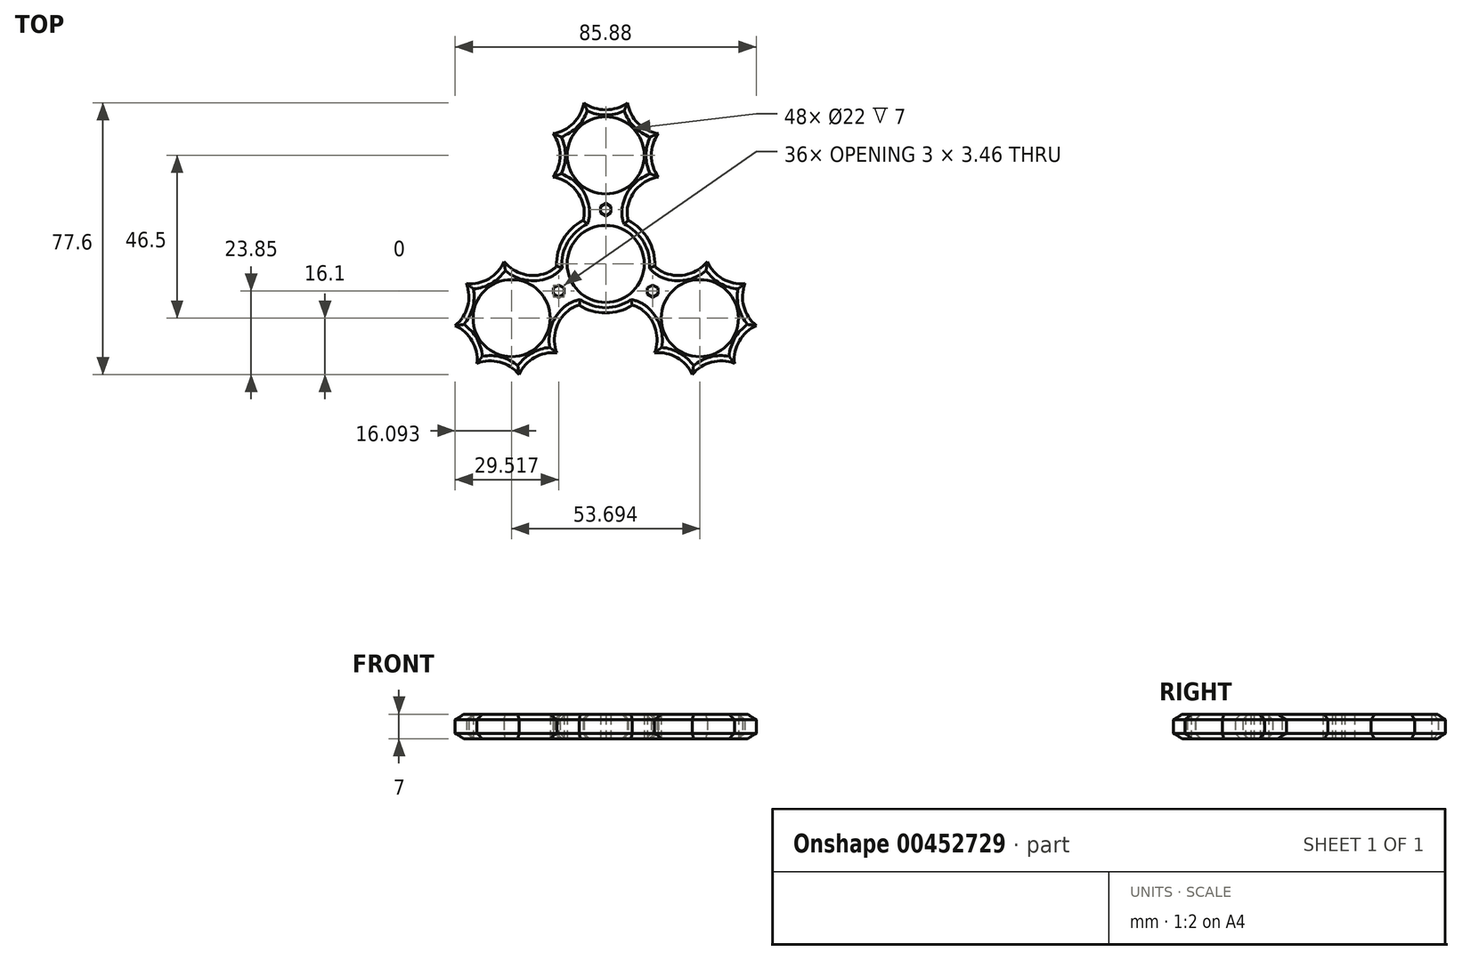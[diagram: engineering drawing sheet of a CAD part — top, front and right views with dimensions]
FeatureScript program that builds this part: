
annotation { "Feature Type Name" : "Feature", "Feature Type Description" : "" }
export const myFeature = defineFeature(function(context is Context, id is Id, definition is map)
    precondition{}
    {
        {
            var Q0;
            Q0=qCreatedBy(makeId("Top.planeOp"),FACE);
            var sketch = newSketch(context, id + "F0", { "sketchPlane" : qUnion([Q0])});
            skCircle(sketch, "E0", {"center": v(0, 0) * mm, "radius": 11 * mm});
            skArc(sketch, "E1.0", {"start": v(-6.44, 12.43) * mm, "mid": v(0, -14) * mm, "end": v(6.44, 12.43) * mm});
            skLineSegment(sketch, "E2", {"start": v(0, 11) * mm, "end": v(0, 20) * mm});
            skCircle(sketch, "E3", {"center": v(0, 31) * mm, "radius": 11 * mm});
            skPoint(sketch, "E4.0.midPoint", {"position": v(0, 45) * mm});
            skLineSegment(sketch, "E5", {"start": v(-15, 24.79) * mm, "end": v(0, 31) * mm});
            skLineSegment(sketch, "E6", {"start": v(-6.21, 16) * mm, "end": v(0, 31) * mm});
            skPoint(sketch, "E7", {"position": v(-9.2, 21.8) * mm});
            skArc(sketch, "E8", {"start": v(-6.21, 16) * mm, "mid": v(-9.2, 21.8) * mm, "end": v(-15, 24.79) * mm});
            skArc(sketch, "E9.1.0", {"start": v(-15, 24.79) * mm, "mid": v(-13, 31) * mm, "end": v(-15, 37.21) * mm});
            skArc(sketch, "E9.2.0", {"start": v(-15, 37.21) * mm, "mid": v(-9.2, 40.2) * mm, "end": v(-6.21, 46) * mm});
            skArc(sketch, "E9.3.0", {"start": v(-6.21, 46) * mm, "mid": v(0, 44) * mm, "end": v(6.21, 46) * mm});
            skArc(sketch, "E9.4.0", {"start": v(6.21, 46) * mm, "mid": v(9.2, 40.2) * mm, "end": v(15, 37.21) * mm});
            skArc(sketch, "E9.5.0", {"start": v(15, 37.21) * mm, "mid": v(13, 31) * mm, "end": v(15, 24.79) * mm});
            skArc(sketch, "E9.6.0", {"start": v(15, 24.79) * mm, "mid": v(9.2, 21.8) * mm, "end": v(6.21, 16) * mm});
            skLineSegment(sketch, "E9.anchor1", {"start": v(0, 31) * mm, "end": v(-16.72, 14.28) * mm, "construction": true});
            skLineSegment(sketch, "E9.anchor2", {"start": v(0, 31) * mm, "end": v(16.72, 14.28) * mm, "construction": true});
            skPoint(sketch, "E10.orphan", {"position": v(-15, 36.21) * mm});
            skPoint(sketch, "E11.orphan", {"position": v(-6.21, 45) * mm});
            skPoint(sketch, "E12.orphan", {"position": v(6.21, 45) * mm});
            skPoint(sketch, "E13.orphan", {"position": v(15, 36.21) * mm});
            skPoint(sketch, "E14.orphan", {"position": v(15, 23.79) * mm});
            skLineSegment(sketch, "E15", {"start": v(9.53, 5.5) * mm, "end": v(12.12, 7) * mm});
            skArc(sketch, "E16", {"start": v(6.21, 16) * mm, "mid": v(7.41, 10.35) * mm, "end": v(12.12, 7) * mm});
            skArc(sketch, "E17.MirrorCS", {"start": v(-6.21, 16) * mm, "mid": v(-7.41, 10.35) * mm, "end": v(-12.12, 7) * mm});
            skArc(sketch, "E18.1.0", {"start": v(-24.73, -31.6) * mm, "mid": v(-30.21, -28.06) * mm, "end": v(-36.73, -28.38) * mm});
            skPoint(sketch, "E18.1.1", {"position": v(-26.85, -15.5) * mm});
            skArc(sketch, "E18.1.2", {"start": v(-42.94, -17.62) * mm, "mid": v(-39.4, -12.14) * mm, "end": v(-39.73, -5.62) * mm});
            skPoint(sketch, "E18.1.3", {"position": v(-42.08, -17.12) * mm});
            skPoint(sketch, "E18.1.4", {"position": v(-28.1, 1.1) * mm});
            skArc(sketch, "E18.1.5", {"start": v(-13.97, -25.38) * mm, "mid": v(-20.35, -26.76) * mm, "end": v(-24.73, -31.6) * mm});
            skArc(sketch, "E18.1.6", {"start": v(-39.73, -5.62) * mm, "mid": v(-33.35, -4.24) * mm, "end": v(-28.97, 0.6) * mm});
            skPoint(sketch, "E18.1.7", {"position": v(-14.29, -18.86) * mm});
            skPoint(sketch, "E18.1.8", {"position": v(-38.97, -22.5) * mm});
            skPoint(sketch, "E18.1.9", {"position": v(-38.86, -5.12) * mm});
            skCircle(sketch, "E18.1.10", {"center": v(-26.85, -15.5) * mm, "radius": 11 * mm});
            skPoint(sketch, "E18.1.11", {"position": v(-23.86, -31.1) * mm});
            skArc(sketch, "E18.1.12", {"start": v(-36.73, -28.38) * mm, "mid": v(-38.1, -22) * mm, "end": v(-42.94, -17.62) * mm});
            skPoint(sketch, "E18.1.13", {"position": v(-35.86, -27.88) * mm});
            skArc(sketch, "E18.1.14", {"start": v(-28.97, 0.6) * mm, "mid": v(-23.48, -2.94) * mm, "end": v(-16.96, -2.62) * mm});
            skArc(sketch, "E18.1.15", {"start": v(-10.75, -13.38) * mm, "mid": v(-14.29, -18.86) * mm, "end": v(-13.97, -25.38) * mm});
            skArc(sketch, "E18.1.16", {"start": v(-10.75, -13.38) * mm, "mid": v(-5.25, -11.6) * mm, "end": v(0, -14) * mm});
            skArc(sketch, "E18.1.17", {"start": v(-16.96, -2.62) * mm, "mid": v(-12.67, 1.25) * mm, "end": v(-12.12, 7) * mm});
            skArc(sketch, "E18.2.0", {"start": v(39.73, -5.62) * mm, "mid": v(39.4, -12.14) * mm, "end": v(42.94, -17.62) * mm});
            skPoint(sketch, "E18.2.1", {"position": v(26.85, -15.5) * mm});
            skArc(sketch, "E18.2.2", {"start": v(36.73, -28.38) * mm, "mid": v(30.21, -28.06) * mm, "end": v(24.73, -31.6) * mm});
            skPoint(sketch, "E18.2.3", {"position": v(35.86, -27.88) * mm});
            skPoint(sketch, "E18.2.4", {"position": v(13.1, -24.88) * mm});
            skArc(sketch, "E18.2.5", {"start": v(28.97, 0.6) * mm, "mid": v(33.35, -4.24) * mm, "end": v(39.73, -5.62) * mm});
            skArc(sketch, "E18.2.6", {"start": v(24.73, -31.6) * mm, "mid": v(20.35, -26.76) * mm, "end": v(13.97, -25.38) * mm});
            skPoint(sketch, "E18.2.7", {"position": v(23.48, -2.94) * mm});
            skPoint(sketch, "E18.2.8", {"position": v(38.97, -22.5) * mm});
            skPoint(sketch, "E18.2.9", {"position": v(23.86, -31.1) * mm});
            skCircle(sketch, "E18.2.10", {"center": v(26.85, -15.5) * mm, "radius": 11 * mm});
            skPoint(sketch, "E18.2.11", {"position": v(38.86, -5.12) * mm});
            skArc(sketch, "E18.2.12", {"start": v(42.94, -17.62) * mm, "mid": v(38.1, -22) * mm, "end": v(36.73, -28.38) * mm});
            skPoint(sketch, "E18.2.13", {"position": v(42.08, -17.12) * mm});
            skArc(sketch, "E18.2.14", {"start": v(13.97, -25.38) * mm, "mid": v(14.29, -18.86) * mm, "end": v(10.75, -13.38) * mm});
            skArc(sketch, "E18.2.15", {"start": v(16.96, -2.62) * mm, "mid": v(23.48, -2.94) * mm, "end": v(28.97, 0.6) * mm});
            skArc(sketch, "E18.2.16", {"start": v(16.96, -2.62) * mm, "mid": v(12.67, 1.25) * mm, "end": v(12.12, 7) * mm});
            skArc(sketch, "E18.2.17", {"start": v(10.75, -13.38) * mm, "mid": v(5.25, -11.6) * mm, "end": v(0, -14) * mm});
            skPoint(sketch, "E19", {"position": v(10.83, 6.25) * mm});
            skPoint(sketch, "E20", {"position": v(6.44, 12.43) * mm});
            skPoint(sketch, "E21", {"position": v(13.99, -0.63) * mm});
            skLineSegment(sketch, "E22.0", {"start": v(1.5, 16.37) * mm, "end": v(1.5, 14.63) * mm});
            skLineSegment(sketch, "E22.1", {"start": v(1.5, 14.63) * mm, "end": v(0, 13.77) * mm});
            skLineSegment(sketch, "E22.2", {"start": v(0, 13.77) * mm, "end": v(-1.5, 14.63) * mm});
            skLineSegment(sketch, "E22.3", {"start": v(-1.5, 14.63) * mm, "end": v(-1.5, 16.37) * mm});
            skLineSegment(sketch, "E22.4", {"start": v(-1.5, 16.37) * mm, "end": v(0, 17.23) * mm});
            skLineSegment(sketch, "E22.5", {"start": v(0, 17.23) * mm, "end": v(1.5, 16.37) * mm});
            skPoint(sketch, "E22.0.midPoint", {"position": v(1.5, 15.5) * mm});
            skLineSegment(sketch, "E23.1.0", {"start": v(-14.92, -8.62) * mm, "end": v(-14.92, -6.88) * mm});
            skLineSegment(sketch, "E23.1.1", {"start": v(-13.42, -9.48) * mm, "end": v(-14.92, -8.62) * mm});
            skLineSegment(sketch, "E23.1.2", {"start": v(-11.92, -8.62) * mm, "end": v(-13.42, -9.48) * mm});
            skLineSegment(sketch, "E23.1.3", {"start": v(-11.92, -6.88) * mm, "end": v(-11.92, -8.62) * mm});
            skLineSegment(sketch, "E23.1.4", {"start": v(-13.42, -6.02) * mm, "end": v(-11.92, -6.88) * mm});
            skLineSegment(sketch, "E23.1.5", {"start": v(-14.92, -6.88) * mm, "end": v(-13.42, -6.02) * mm});
            skLineSegment(sketch, "E23.2.0", {"start": v(14.92, -8.62) * mm, "end": v(13.42, -9.48) * mm});
            skLineSegment(sketch, "E23.2.1", {"start": v(14.92, -6.88) * mm, "end": v(14.92, -8.62) * mm});
            skLineSegment(sketch, "E23.2.2", {"start": v(13.42, -6.02) * mm, "end": v(14.92, -6.88) * mm});
            skLineSegment(sketch, "E23.2.3", {"start": v(11.92, -6.88) * mm, "end": v(13.42, -6.02) * mm});
            skLineSegment(sketch, "E23.2.4", {"start": v(11.92, -8.62) * mm, "end": v(11.92, -6.88) * mm});
            skLineSegment(sketch, "E23.2.5", {"start": v(13.42, -9.48) * mm, "end": v(11.92, -8.62) * mm});
            skSolve(sketch);
        }
        {
            var Q0;
            {var subQ5=sQuery(id+"F0.wireOp",EDGE,"E9.1.0");Q0=makeQuery(id+"F0.imprint","IMPRINT",FACE,{"disambiguationData":[TD([[makeQuery(id+"F0.imprint","IMPRINT",EDGE,{"derivedFrom":subQ5}),-1.0]])]});}
            var Q1;
            {var subQ5=sQuery(id+"F0.wireOp",EDGE,"E8");Q1=makeQuery(id+"F0.imprint","IMPRINT",FACE,{"disambiguationData":[TD([[makeQuery(id+"F0.imprint","IMPRINT",EDGE,{"derivedFrom":subQ5}),-1.0]])]});}
            var Q2;
            {var subQ0=sQuery(id+"F0.wireOp",EDGE,"E17.MirrorCS");var subQ7=sQuery(id+"F0.wireOp",EDGE,"E1.0");var subQ9=makeQuery(id+"F0.imprint","INTERSECT",VERTEX,{"derivedFrom":[subQ7,subQ0]});Q2=makeQuery(id+"F0.imprint","IMPRINT",FACE,{"disambiguationData":[TD([[makeQuery(id+"F0.imprint","IMPRINT",EDGE,{"disambiguationData":[TD([[subQ9,1.0]])],"derivedFrom":subQ7}),-1.0]])]});}
            var Q3;
            {var subQ1=sQuery(id+"F0.wireOp",EDGE,"E15");Q3=makeQuery(id+"F0.imprint","IMPRINT",FACE,{"disambiguationData":[TD([[makeQuery(id+"F0.imprint","IMPRINT",EDGE,{"derivedFrom":subQ1}),-1.0]])]});}
            var Q4;
            {var subQ0=sQuery(id+"F0.wireOp",EDGE,"E15");Q4=makeQuery(id+"F0.imprint","IMPRINT",FACE,{"disambiguationData":[TD([[makeQuery(id+"F0.imprint","IMPRINT",EDGE,{"derivedFrom":subQ0}),1.0]])]});}
            var Q5;
            Q5=makeQuery(id+"F0.imprint","IMPRINT",FACE,{"disambiguationData":[TD([[makeQuery(id+"F0.imprint","IMPRINT",EDGE,{"derivedFrom":sQuery(id+"F0.wireOp",EDGE,"E18.2.0")}),-1.0]])]});
            var Q6;
            Q6=makeQuery(id+"F0.imprint","IMPRINT",FACE,{"disambiguationData":[TD([[makeQuery(id+"F0.imprint","IMPRINT",EDGE,{"derivedFrom":sQuery(id+"F0.wireOp",EDGE,"E18.1.0")}),-1.0]])]});
            var Q7;
            {var subQ0=sQuery(id+"F0.wireOp",EDGE,"E17.MirrorCS");var subQ1=sQuery(id+"F0.wireOp",EDGE,"E1.0");var subQ3=makeQuery(id+"F0.imprint","INTERSECT",VERTEX,{"derivedFrom":[subQ1,subQ0]});Q7=makeQuery(id+"F0.imprint","IMPRINT",FACE,{"disambiguationData":[TD([[makeQuery(id+"F0.imprint","IMPRINT",EDGE,{"disambiguationData":[TD([[subQ3,-1.0]])],"derivedFrom":subQ1}),1.0]])]});}
            var Q8;
            {var subQ0=sQuery(id+"F0.wireOp",EDGE,"E18.1.17");var subQ1=sQuery(id+"F0.wireOp",EDGE,"E1.0");var subQ3=makeQuery(id+"F0.imprint","INTERSECT",VERTEX,{"derivedFrom":[subQ1,subQ0]});Q8=makeQuery(id+"F0.imprint","IMPRINT",FACE,{"disambiguationData":[TD([[makeQuery(id+"F0.imprint","IMPRINT",EDGE,{"disambiguationData":[TD([[subQ3,1.0]])],"derivedFrom":subQ1}),1.0]])]});}
            var Q9;
            {var subQ0=sQuery(id+"F0.wireOp",EDGE,"E18.1.16");var subQ1=sQuery(id+"F0.wireOp",EDGE,"E1.0");var subQ3=makeQuery(id+"F0.imprint","INTERSECT",VERTEX,{"derivedFrom":[subQ1,subQ0]});Q9=makeQuery(id+"F0.imprint","IMPRINT",FACE,{"disambiguationData":[TD([[makeQuery(id+"F0.imprint","IMPRINT",EDGE,{"disambiguationData":[TD([[subQ3,-1.0]])],"derivedFrom":subQ1}),1.0]])]});}
            var Q10;
            {var subQ0=sQuery(id+"F0.wireOp",EDGE,"E18.2.17");var subQ1=sQuery(id+"F0.wireOp",EDGE,"E1.0");var subQ3=makeQuery(id+"F0.imprint","INTERSECT",VERTEX,{"derivedFrom":[subQ1,subQ0]});Q10=makeQuery(id+"F0.imprint","IMPRINT",FACE,{"disambiguationData":[TD([[makeQuery(id+"F0.imprint","IMPRINT",EDGE,{"disambiguationData":[TD([[subQ3,1.0]])],"derivedFrom":subQ1}),1.0]])]});}
            var Q11;
            {var subQ0=sQuery(id+"F0.wireOp",EDGE,"E16");var subQ1=sQuery(id+"F0.wireOp",EDGE,"E1.0");var subQ3=makeQuery(id+"F0.imprint","INTERSECT",VERTEX,{"derivedFrom":[subQ1,subQ0]});Q11=makeQuery(id+"F0.imprint","IMPRINT",FACE,{"disambiguationData":[TD([[makeQuery(id+"F0.imprint","IMPRINT",EDGE,{"disambiguationData":[TD([[subQ3,1.0]])],"derivedFrom":subQ1}),1.0]])]});}
            var Q12;
            {var subQ0=sQuery(id+"F0.wireOp",EDGE,"E18.2.16");var subQ1=sQuery(id+"F0.wireOp",EDGE,"E1.0");var subQ3=makeQuery(id+"F0.imprint","INTERSECT",VERTEX,{"derivedFrom":[subQ1,subQ0]});Q12=makeQuery(id+"F0.imprint","IMPRINT",FACE,{"disambiguationData":[TD([[makeQuery(id+"F0.imprint","IMPRINT",EDGE,{"disambiguationData":[TD([[subQ3,-1.0]])],"derivedFrom":subQ1}),1.0]])]});}
            extrude(context, id + "F1", {"entities" : qUnion([Q0, Q1, Q2, Q3, Q4, Q5, Q6, Q7, Q8, Q9, Q10, Q11, Q12]), "endBound" : BoundingType.SYMMETRIC, "depth" : 7 * mm});
        }
        {
            var Q0;
            Q0=makeQuery(id+"F1.opExtrude","CAP_EDGE",EDGE,{"disambiguationData":[OSD([sQuery(id+"F0.wireOp",EDGE,"E8")])],"isStart":false});
            var Q1;
            Q1=makeQuery(id+"F1.opExtrude","CAP_EDGE",EDGE,{"disambiguationData":[OSD([sQuery(id+"F0.wireOp",EDGE,"E9.1.0")])],"isStart":false});
            var Q2;
            Q2=makeQuery(id+"F1.opExtrude","CAP_EDGE",EDGE,{"disambiguationData":[OSD([sQuery(id+"F0.wireOp",EDGE,"E9.2.0")])],"isStart":false});
            var Q3;
            Q3=makeQuery(id+"F1.opExtrude","CAP_EDGE",EDGE,{"disambiguationData":[OSD([sQuery(id+"F0.wireOp",EDGE,"E9.3.0")])],"isStart":false});
            var Q4;
            Q4=makeQuery(id+"F1.opExtrude","CAP_EDGE",EDGE,{"disambiguationData":[OSD([sQuery(id+"F0.wireOp",EDGE,"E9.4.0")])],"isStart":false});
            var Q5;
            Q5=makeQuery(id+"F1.opExtrude","CAP_EDGE",EDGE,{"disambiguationData":[OSD([sQuery(id+"F0.wireOp",EDGE,"E9.5.0")])],"isStart":false});
            var Q6;
            Q6=makeQuery(id+"F1.opExtrude","CAP_EDGE",EDGE,{"disambiguationData":[OSD([sQuery(id+"F0.wireOp",EDGE,"E9.6.0")])],"isStart":false});
            var Q7;
            Q7=makeQuery(id+"F1.opExtrude","CAP_EDGE",EDGE,{"disambiguationData":[OSD([sQuery(id+"F0.wireOp",EDGE,"E16")])],"isStart":false});
            var Q8;
            {var subQ0=sQuery(id+"F0.wireOp",EDGE,"E18.2.16");var subQ1=sQuery(id+"F0.wireOp",EDGE,"E16");var subQ2=sQuery(id+"F0.wireOp",EDGE,"E1.0");Q8=makeQuery(id+"F1.opExtrude","CAP_EDGE",EDGE,{"disambiguationData":[OSD([subQ2]),TDD([makeQuery(id+"F0.imprint","IMPRINT",EDGE,{"disambiguationData":[TD([[makeQuery(id+"F0.imprint","INTERSECT",VERTEX,{"derivedFrom":[subQ2,subQ1]}),1.0]])],"derivedFrom":subQ2}),makeQuery(id+"F0.imprint","IMPRINT",EDGE,{"disambiguationData":[TD([[makeQuery(id+"F0.imprint","INTERSECT",VERTEX,{"derivedFrom":[subQ2,subQ0]}),-1.0]])],"derivedFrom":subQ2})])],"isStart":false});}
            var Q9;
            Q9=makeQuery(id+"F1.opExtrude","CAP_EDGE",EDGE,{"disambiguationData":[OSD([sQuery(id+"F0.wireOp",EDGE,"E18.2.16")])],"isStart":false});
            var Q10;
            Q10=makeQuery(id+"F1.opExtrude","CAP_EDGE",EDGE,{"disambiguationData":[OSD([sQuery(id+"F0.wireOp",EDGE,"E18.2.15")])],"isStart":false});
            var Q11;
            Q11=makeQuery(id+"F1.opExtrude","CAP_EDGE",EDGE,{"disambiguationData":[OSD([sQuery(id+"F0.wireOp",EDGE,"E18.2.5")])],"isStart":false});
            var Q12;
            Q12=makeQuery(id+"F1.opExtrude","CAP_EDGE",EDGE,{"disambiguationData":[OSD([sQuery(id+"F0.wireOp",EDGE,"E18.2.0")])],"isStart":false});
            var Q13;
            Q13=makeQuery(id+"F1.opExtrude","CAP_EDGE",EDGE,{"disambiguationData":[OSD([sQuery(id+"F0.wireOp",EDGE,"E18.2.12")])],"isStart":false});
            var Q14;
            Q14=makeQuery(id+"F1.opExtrude","CAP_EDGE",EDGE,{"disambiguationData":[OSD([sQuery(id+"F0.wireOp",EDGE,"E18.2.2")])],"isStart":false});
            var Q15;
            Q15=makeQuery(id+"F1.opExtrude","CAP_EDGE",EDGE,{"disambiguationData":[OSD([sQuery(id+"F0.wireOp",EDGE,"E18.2.6")])],"isStart":false});
            var Q16;
            Q16=makeQuery(id+"F1.opExtrude","CAP_EDGE",EDGE,{"disambiguationData":[OSD([sQuery(id+"F0.wireOp",EDGE,"E18.2.14")])],"isStart":false});
            var Q17;
            Q17=makeQuery(id+"F1.opExtrude","CAP_EDGE",EDGE,{"disambiguationData":[OSD([sQuery(id+"F0.wireOp",EDGE,"E18.2.17")])],"isStart":false});
            var Q18;
            {var subQ0=sQuery(id+"F0.wireOp",EDGE,"E18.2.17");var subQ1=sQuery(id+"F0.wireOp",EDGE,"E18.1.16");var subQ2=sQuery(id+"F0.wireOp",EDGE,"E1.0");Q18=makeQuery(id+"F1.opExtrude","CAP_EDGE",EDGE,{"disambiguationData":[OSD([subQ2]),TDD([makeQuery(id+"F0.imprint","IMPRINT",EDGE,{"disambiguationData":[TD([[makeQuery(id+"F0.imprint","INTERSECT",VERTEX,{"derivedFrom":[subQ2,subQ1]}),-1.0]])],"derivedFrom":subQ2}),makeQuery(id+"F0.imprint","IMPRINT",EDGE,{"disambiguationData":[TD([[makeQuery(id+"F0.imprint","INTERSECT",VERTEX,{"derivedFrom":[subQ2,subQ0]}),1.0]])],"derivedFrom":subQ2})])],"isStart":false});}
            var Q19;
            Q19=makeQuery(id+"F1.opExtrude","CAP_EDGE",EDGE,{"disambiguationData":[OSD([sQuery(id+"F0.wireOp",EDGE,"E18.1.16")])],"isStart":false});
            var Q20;
            Q20=makeQuery(id+"F1.opExtrude","CAP_EDGE",EDGE,{"disambiguationData":[OSD([sQuery(id+"F0.wireOp",EDGE,"E18.1.15")])],"isStart":false});
            var Q21;
            Q21=makeQuery(id+"F1.opExtrude","CAP_EDGE",EDGE,{"disambiguationData":[OSD([sQuery(id+"F0.wireOp",EDGE,"E18.1.5")])],"isStart":false});
            var Q22;
            Q22=makeQuery(id+"F1.opExtrude","CAP_EDGE",EDGE,{"disambiguationData":[OSD([sQuery(id+"F0.wireOp",EDGE,"E18.1.0")])],"isStart":false});
            var Q23;
            Q23=makeQuery(id+"F1.opExtrude","CAP_EDGE",EDGE,{"disambiguationData":[OSD([sQuery(id+"F0.wireOp",EDGE,"E18.1.12")])],"isStart":false});
            var Q24;
            Q24=makeQuery(id+"F1.opExtrude","CAP_EDGE",EDGE,{"disambiguationData":[OSD([sQuery(id+"F0.wireOp",EDGE,"E18.1.2")])],"isStart":false});
            var Q25;
            Q25=makeQuery(id+"F1.opExtrude","CAP_EDGE",EDGE,{"disambiguationData":[OSD([sQuery(id+"F0.wireOp",EDGE,"E18.1.6")])],"isStart":false});
            var Q26;
            Q26=makeQuery(id+"F1.opExtrude","CAP_EDGE",EDGE,{"disambiguationData":[OSD([sQuery(id+"F0.wireOp",EDGE,"E18.1.14")])],"isStart":false});
            var Q27;
            Q27=makeQuery(id+"F1.opExtrude","CAP_EDGE",EDGE,{"disambiguationData":[OSD([sQuery(id+"F0.wireOp",EDGE,"E18.1.17")])],"isStart":false});
            var Q28;
            {var subQ0=sQuery(id+"F0.wireOp",EDGE,"E18.1.17");var subQ1=sQuery(id+"F0.wireOp",EDGE,"E17.MirrorCS");var subQ2=sQuery(id+"F0.wireOp",EDGE,"E1.0");Q28=makeQuery(id+"F1.opExtrude","CAP_EDGE",EDGE,{"disambiguationData":[OSD([subQ2]),TDD([makeQuery(id+"F0.imprint","IMPRINT",EDGE,{"disambiguationData":[TD([[makeQuery(id+"F0.imprint","INTERSECT",VERTEX,{"derivedFrom":[subQ2,subQ1]}),-1.0]])],"derivedFrom":subQ2}),makeQuery(id+"F0.imprint","IMPRINT",EDGE,{"disambiguationData":[TD([[makeQuery(id+"F0.imprint","INTERSECT",VERTEX,{"derivedFrom":[subQ2,subQ0]}),1.0]])],"derivedFrom":subQ2})])],"isStart":false});}
            var Q29;
            Q29=makeQuery(id+"F1.opExtrude","CAP_EDGE",EDGE,{"disambiguationData":[OSD([sQuery(id+"F0.wireOp",EDGE,"E17.MirrorCS")])],"isStart":false});
            var Q30;
            {var subQ0=sQuery(id+"F0.wireOp",EDGE,"E18.2.17");var subQ1=sQuery(id+"F0.wireOp",EDGE,"E18.1.16");var subQ2=sQuery(id+"F0.wireOp",EDGE,"E1.0");Q30=makeQuery(id+"F1.opExtrude","CAP_EDGE",EDGE,{"disambiguationData":[OSD([subQ2]),TDD([makeQuery(id+"F0.imprint","IMPRINT",EDGE,{"disambiguationData":[TD([[makeQuery(id+"F0.imprint","INTERSECT",VERTEX,{"derivedFrom":[subQ2,subQ1]}),-1.0]])],"derivedFrom":subQ2}),makeQuery(id+"F0.imprint","IMPRINT",EDGE,{"disambiguationData":[TD([[makeQuery(id+"F0.imprint","INTERSECT",VERTEX,{"derivedFrom":[subQ2,subQ0]}),1.0]])],"derivedFrom":subQ2})])],"isStart":true});}
            var Q31;
            Q31=makeQuery(id+"F1.opExtrude","CAP_EDGE",EDGE,{"disambiguationData":[OSD([sQuery(id+"F0.wireOp",EDGE,"E18.2.17")])],"isStart":true});
            var Q32;
            Q32=makeQuery(id+"F1.opExtrude","CAP_EDGE",EDGE,{"disambiguationData":[OSD([sQuery(id+"F0.wireOp",EDGE,"E18.2.14")])],"isStart":true});
            var Q33;
            Q33=makeQuery(id+"F1.opExtrude","CAP_EDGE",EDGE,{"disambiguationData":[OSD([sQuery(id+"F0.wireOp",EDGE,"E18.2.6")])],"isStart":true});
            var Q34;
            Q34=makeQuery(id+"F1.opExtrude","CAP_EDGE",EDGE,{"disambiguationData":[OSD([sQuery(id+"F0.wireOp",EDGE,"E18.2.2")])],"isStart":true});
            var Q35;
            Q35=makeQuery(id+"F1.opExtrude","CAP_EDGE",EDGE,{"disambiguationData":[OSD([sQuery(id+"F0.wireOp",EDGE,"E18.2.12")])],"isStart":true});
            var Q36;
            Q36=makeQuery(id+"F1.opExtrude","CAP_EDGE",EDGE,{"disambiguationData":[OSD([sQuery(id+"F0.wireOp",EDGE,"E18.2.0")])],"isStart":true});
            var Q37;
            Q37=makeQuery(id+"F1.opExtrude","CAP_EDGE",EDGE,{"disambiguationData":[OSD([sQuery(id+"F0.wireOp",EDGE,"E18.2.5")])],"isStart":true});
            var Q38;
            Q38=makeQuery(id+"F1.opExtrude","CAP_EDGE",EDGE,{"disambiguationData":[OSD([sQuery(id+"F0.wireOp",EDGE,"E18.2.15")])],"isStart":true});
            var Q39;
            Q39=makeQuery(id+"F1.opExtrude","CAP_EDGE",EDGE,{"disambiguationData":[OSD([sQuery(id+"F0.wireOp",EDGE,"E18.2.16")])],"isStart":true});
            var Q40;
            {var subQ0=sQuery(id+"F0.wireOp",EDGE,"E18.2.16");var subQ1=sQuery(id+"F0.wireOp",EDGE,"E16");var subQ2=sQuery(id+"F0.wireOp",EDGE,"E1.0");Q40=makeQuery(id+"F1.opExtrude","CAP_EDGE",EDGE,{"disambiguationData":[OSD([subQ2]),TDD([makeQuery(id+"F0.imprint","IMPRINT",EDGE,{"disambiguationData":[TD([[makeQuery(id+"F0.imprint","INTERSECT",VERTEX,{"derivedFrom":[subQ2,subQ1]}),1.0]])],"derivedFrom":subQ2}),makeQuery(id+"F0.imprint","IMPRINT",EDGE,{"disambiguationData":[TD([[makeQuery(id+"F0.imprint","INTERSECT",VERTEX,{"derivedFrom":[subQ2,subQ0]}),-1.0]])],"derivedFrom":subQ2})])],"isStart":true});}
            var Q41;
            Q41=makeQuery(id+"F1.opExtrude","CAP_EDGE",EDGE,{"disambiguationData":[OSD([sQuery(id+"F0.wireOp",EDGE,"E16")])],"isStart":true});
            var Q42;
            Q42=makeQuery(id+"F1.opExtrude","CAP_EDGE",EDGE,{"disambiguationData":[OSD([sQuery(id+"F0.wireOp",EDGE,"E9.6.0")])],"isStart":true});
            var Q43;
            Q43=makeQuery(id+"F1.opExtrude","CAP_EDGE",EDGE,{"disambiguationData":[OSD([sQuery(id+"F0.wireOp",EDGE,"E9.5.0")])],"isStart":true});
            var Q44;
            Q44=makeQuery(id+"F1.opExtrude","CAP_EDGE",EDGE,{"disambiguationData":[OSD([sQuery(id+"F0.wireOp",EDGE,"E9.4.0")])],"isStart":true});
            var Q45;
            Q45=makeQuery(id+"F1.opExtrude","CAP_EDGE",EDGE,{"disambiguationData":[OSD([sQuery(id+"F0.wireOp",EDGE,"E9.3.0")])],"isStart":true});
            var Q46;
            Q46=makeQuery(id+"F1.opExtrude","CAP_EDGE",EDGE,{"disambiguationData":[OSD([sQuery(id+"F0.wireOp",EDGE,"E9.2.0")])],"isStart":true});
            var Q47;
            Q47=makeQuery(id+"F1.opExtrude","CAP_EDGE",EDGE,{"disambiguationData":[OSD([sQuery(id+"F0.wireOp",EDGE,"E9.1.0")])],"isStart":true});
            var Q48;
            Q48=makeQuery(id+"F1.opExtrude","CAP_EDGE",EDGE,{"disambiguationData":[OSD([sQuery(id+"F0.wireOp",EDGE,"E8")])],"isStart":true});
            var Q49;
            Q49=makeQuery(id+"F1.opExtrude","CAP_EDGE",EDGE,{"disambiguationData":[OSD([sQuery(id+"F0.wireOp",EDGE,"E17.MirrorCS")])],"isStart":true});
            var Q50;
            {var subQ0=sQuery(id+"F0.wireOp",EDGE,"E18.1.17");var subQ1=sQuery(id+"F0.wireOp",EDGE,"E17.MirrorCS");var subQ2=sQuery(id+"F0.wireOp",EDGE,"E1.0");Q50=makeQuery(id+"F1.opExtrude","CAP_EDGE",EDGE,{"disambiguationData":[OSD([subQ2]),TDD([makeQuery(id+"F0.imprint","IMPRINT",EDGE,{"disambiguationData":[TD([[makeQuery(id+"F0.imprint","INTERSECT",VERTEX,{"derivedFrom":[subQ2,subQ1]}),-1.0]])],"derivedFrom":subQ2}),makeQuery(id+"F0.imprint","IMPRINT",EDGE,{"disambiguationData":[TD([[makeQuery(id+"F0.imprint","INTERSECT",VERTEX,{"derivedFrom":[subQ2,subQ0]}),1.0]])],"derivedFrom":subQ2})])],"isStart":true});}
            var Q51;
            Q51=makeQuery(id+"F1.opExtrude","CAP_EDGE",EDGE,{"disambiguationData":[OSD([sQuery(id+"F0.wireOp",EDGE,"E18.1.17")])],"isStart":true});
            var Q52;
            Q52=makeQuery(id+"F1.opExtrude","CAP_EDGE",EDGE,{"disambiguationData":[OSD([sQuery(id+"F0.wireOp",EDGE,"E18.1.14")])],"isStart":true});
            var Q53;
            Q53=makeQuery(id+"F1.opExtrude","CAP_EDGE",EDGE,{"disambiguationData":[OSD([sQuery(id+"F0.wireOp",EDGE,"E18.1.6")])],"isStart":true});
            var Q54;
            Q54=makeQuery(id+"F1.opExtrude","CAP_EDGE",EDGE,{"disambiguationData":[OSD([sQuery(id+"F0.wireOp",EDGE,"E18.1.2")])],"isStart":true});
            var Q55;
            Q55=makeQuery(id+"F1.opExtrude","CAP_EDGE",EDGE,{"disambiguationData":[OSD([sQuery(id+"F0.wireOp",EDGE,"E18.1.12")])],"isStart":true});
            var Q56;
            Q56=makeQuery(id+"F1.opExtrude","CAP_EDGE",EDGE,{"disambiguationData":[OSD([sQuery(id+"F0.wireOp",EDGE,"E18.1.0")])],"isStart":true});
            var Q57;
            Q57=makeQuery(id+"F1.opExtrude","CAP_EDGE",EDGE,{"disambiguationData":[OSD([sQuery(id+"F0.wireOp",EDGE,"E18.1.5")])],"isStart":true});
            var Q58;
            Q58=makeQuery(id+"F1.opExtrude","CAP_EDGE",EDGE,{"disambiguationData":[OSD([sQuery(id+"F0.wireOp",EDGE,"E18.1.15")])],"isStart":true});
            var Q59;
            Q59=makeQuery(id+"F1.opExtrude","CAP_EDGE",EDGE,{"disambiguationData":[OSD([sQuery(id+"F0.wireOp",EDGE,"E18.1.16")])],"isStart":true});
            chamfer(context, id + "F2", {"entities" : qUnion([Q0, Q1, Q2, Q3, Q4, Q5, Q6, Q7, Q8, Q9, Q10, Q11, Q12, Q13, Q14, Q15, Q16, Q17, Q18, Q19, Q20, Q21, Q22, Q23, Q24, Q25, Q26, Q27, Q28, Q29, Q30, Q31, Q32, Q33, Q34, Q35, Q36, Q37, Q38, Q39, Q40, Q41, Q42, Q43, Q44, Q45, Q46, Q47, Q48, Q49, Q50, Q51, Q52, Q53, Q54, Q55, Q56, Q57, Q58, Q59]), "width" : 1.5 * mm, "tangentPropagation" : true});
        }
    });
